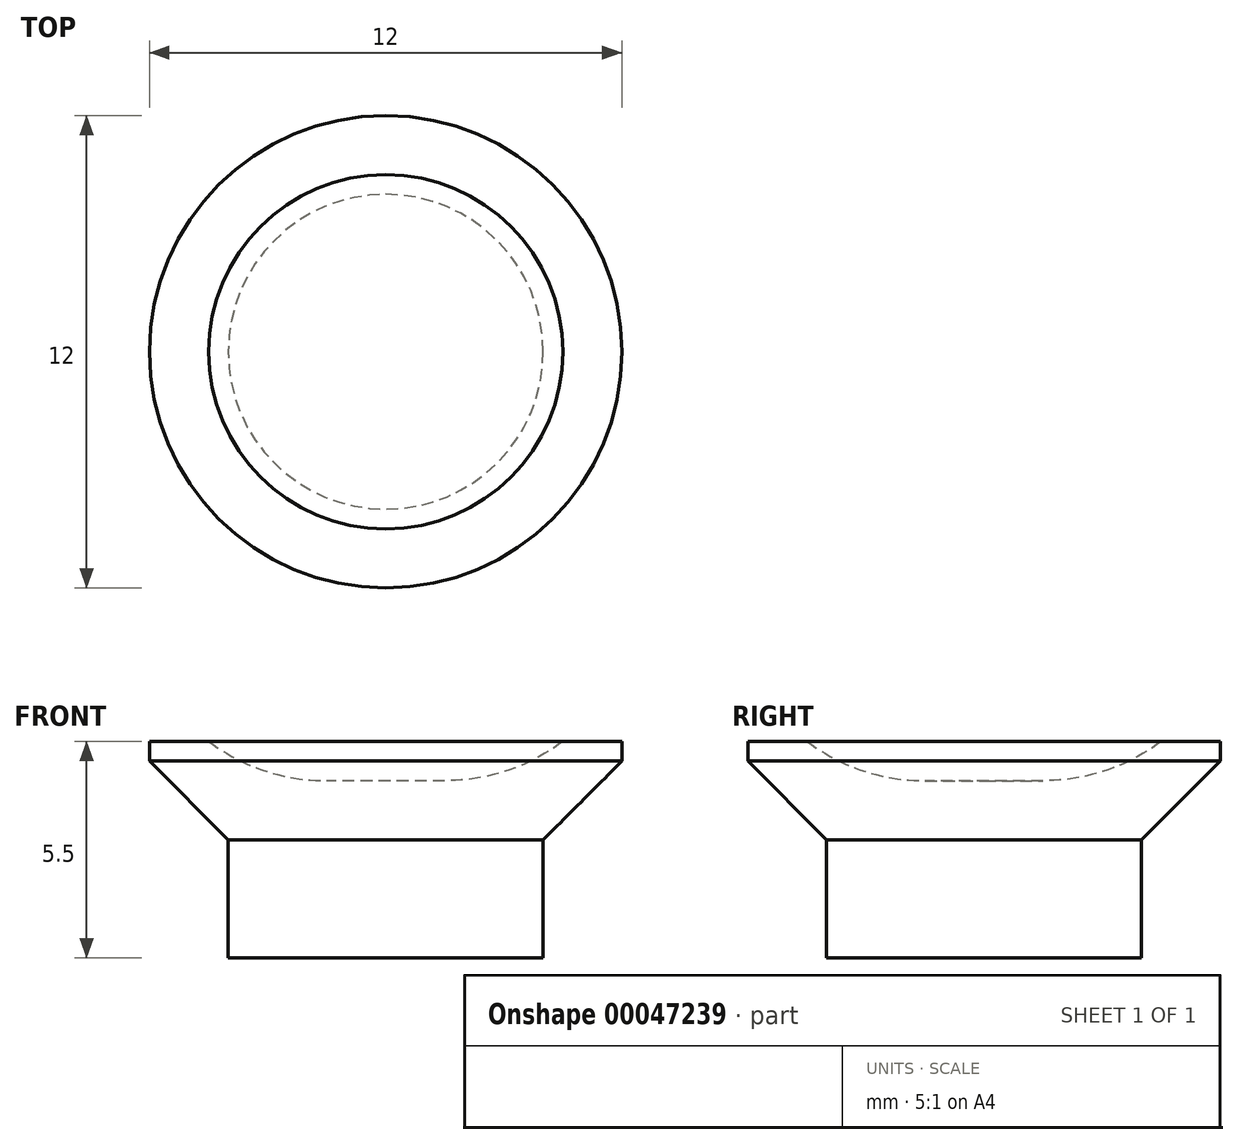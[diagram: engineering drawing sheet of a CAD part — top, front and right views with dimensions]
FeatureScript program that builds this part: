
annotation { "Feature Type Name" : "Feature", "Feature Type Description" : "" }
export const myFeature = defineFeature(function(context is Context, id is Id, definition is map)
    precondition{}
    {
        {
            var Q0;
            Q0=qCreatedBy(makeId("Top.planeOp"),FACE);
            var sketch = newSketch(context, id + "F0", { "sketchPlane" : qUnion([Q0])});
            skCircle(sketch, "E0", {"center": v(0, 0) * mm, "radius": 4 * mm});
            skSolve(sketch);
        }
        {
            var Q0;
            Q0 = qSketchRegion(id + "F0", true);
            extrude(context, id + "F1", {"entities" : qUnion([Q0]), "depth" : 3 * mm});
        }
        {
            var Q0;
            Q0=makeQuery(id+"F1.opExtrude","CAP_FACE",FACE,{"disambiguationData":[OSD([sQuery(id+"F0.wireOp",EDGE,"E0")])],"isStart":false});
            var sketch = newSketch(context, id + "F2", { "sketchPlane" : qUnion([Q0])});
            skCircle(sketch, "E1", {"center": v(0, 0) * mm, "radius": 6 * mm});
            skSolve(sketch);
        }
        {
            var Q0;
            Q0 = qSketchRegion(id + "F2", true);
            extrude(context, id + "F3", {"entities" : qUnion([Q0]), "operationType" : NewBodyOperationType.ADD, "depth" : 2.5 * mm});
        }
        {
            var Q0;
            Q0=makeQuery(id+"F3.opExtrude","CAP_EDGE",EDGE,{"disambiguationData":[OSD([sQuery(id+"F2.wireOp",EDGE,"E1")])],"isStart":true});
            chamfer(context, id + "F4", {"entities" : qUnion([Q0]), "width" : 2 * mm, "tangentPropagation" : true});
        }
        {
            var Q0;
            Q0=makeQuery(id+"F3.opExtrude","CAP_FACE",FACE,{"disambiguationData":[OSD([sQuery(id+"F2.wireOp",EDGE,"E1")])],"isStart":false});
            var sketch = newSketch(context, id + "F5", { "sketchPlane" : qUnion([Q0])});
            skCircle(sketch, "E2", {"center": v(0, 0) * mm, "radius": 4.5 * mm});
            skSolve(sketch);
        }
        {
            var Q0;
            Q0 = qSketchRegion(id + "F5", true);
            extrude(context, id + "F6", {"entities" : qUnion([Q0]), "operationType" : NewBodyOperationType.REMOVE, "oppositeDirection" : true, "depth" : 1 * mm});
        }
        {
            var Q0;
            Q0=makeQuery(id+"F6.boolean.opBoolean","COPY",EDGE,{"derivedFrom":makeQuery(id+"F6.opExtrude","CAP_EDGE",EDGE,{"disambiguationData":[OSD([sQuery(id+"F5.wireOp",EDGE,"E2")])],"isStart":false})});
            fillet(context, id + "F7", {"entities" : qUnion([Q0]), "radius" : 5 * mm, "tangentPropagation" : true, "allowEdgeOverflow" : false});
        }
    });
